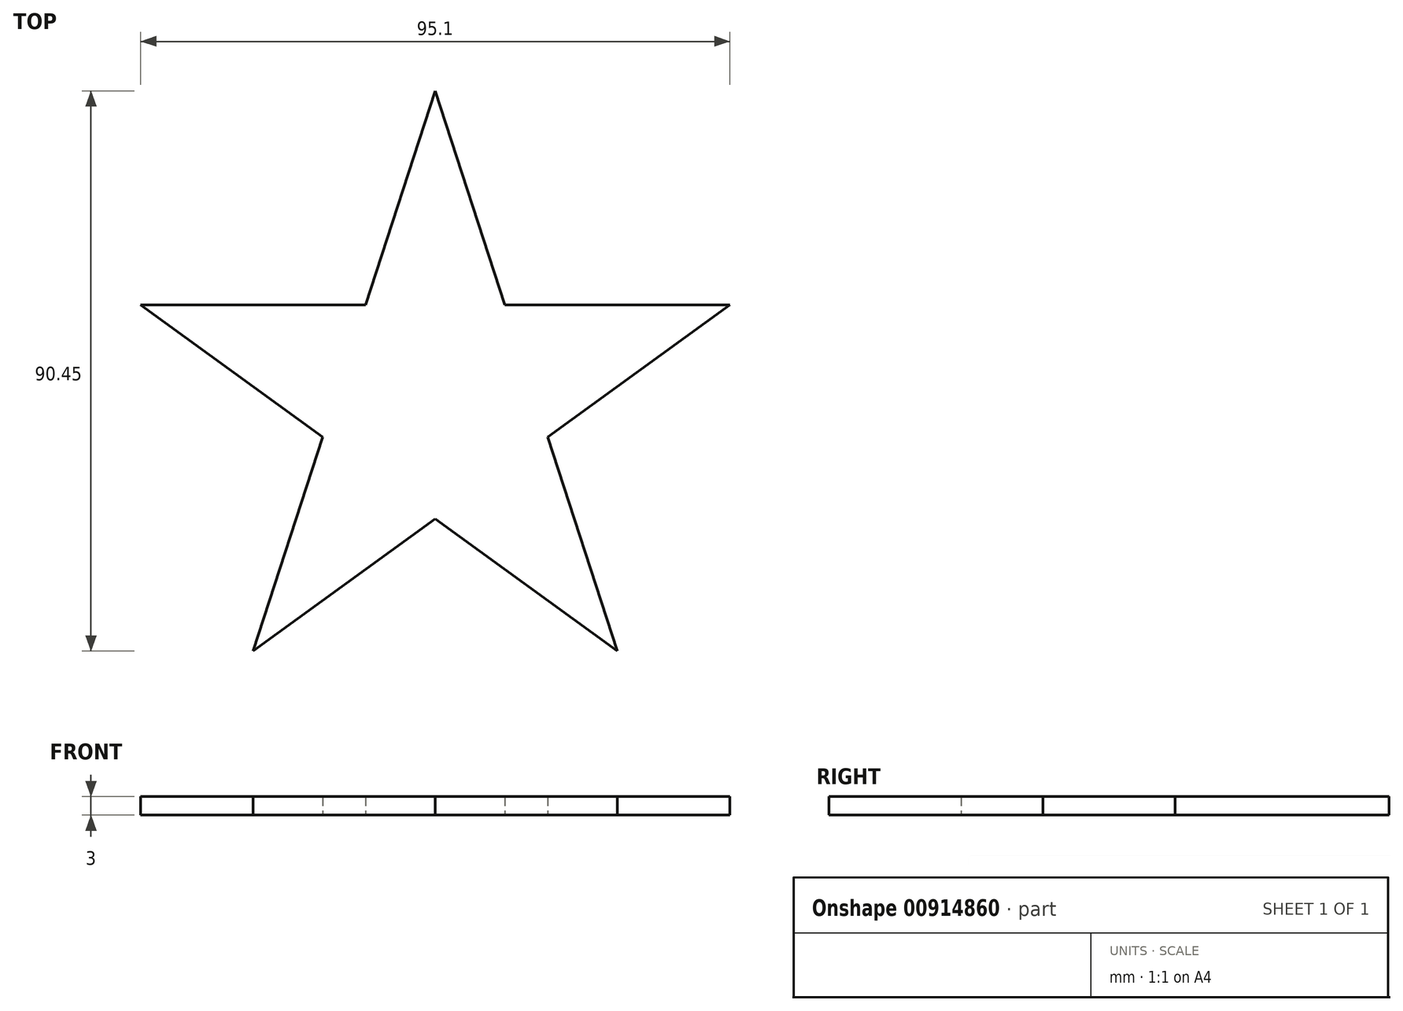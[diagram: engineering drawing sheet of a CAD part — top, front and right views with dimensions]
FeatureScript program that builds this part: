
annotation { "Feature Type Name" : "Feature", "Feature Type Description" : "" }
export const myFeature = defineFeature(function(context is Context, id is Id, definition is map)
    precondition{}
    {
        {
            var Q0;
            Q0=qCreatedBy(makeId("Top.planeOp"),FACE);
            var sketch = newSketch(context, id + "F0", { "sketchPlane" : qUnion([Q0])});
            skCircle(sketch, "E0", {"center": v(0, 0) * mm, "radius": 50 * mm});
            skPoint(sketch, "E1", {"position": v(0, 50) * mm});
            skPoint(sketch, "E2", {"position": v(47.55, 15.45) * mm});
            skPoint(sketch, "E3", {"position": v(29.39, -40.45) * mm});
            skPoint(sketch, "E4", {"position": v(-29.39, -40.45) * mm});
            skPoint(sketch, "E5", {"position": v(-47.55, 15.45) * mm});
            skLineSegment(sketch, "E6", {"start": v(0, 50) * mm, "end": v(0, 0) * mm});
            skLineSegment(sketch, "E7", {"start": v(47.55, 15.45) * mm, "end": v(0, 0) * mm});
            skLineSegment(sketch, "E8", {"start": v(29.39, -40.45) * mm, "end": v(0, 0) * mm});
            skLineSegment(sketch, "E9", {"start": v(-29.39, -40.45) * mm, "end": v(0, 0) * mm});
            skLineSegment(sketch, "E10", {"start": v(-47.55, 15.45) * mm, "end": v(0, 0) * mm});
            skLineSegment(sketch, "E11", {"start": v(-29.39, -40.45) * mm, "end": v(0, 50) * mm});
            skLineSegment(sketch, "E12", {"start": v(0, 50) * mm, "end": v(29.39, -40.45) * mm});
            skLineSegment(sketch, "E13", {"start": v(29.39, -40.45) * mm, "end": v(-47.55, 15.45) * mm});
            skLineSegment(sketch, "E14", {"start": v(-47.55, 15.45) * mm, "end": v(47.55, 15.45) * mm});
            skLineSegment(sketch, "E15", {"start": v(47.55, 15.45) * mm, "end": v(-29.39, -40.45) * mm});
            skSolve(sketch);
        }
        {
            var Q0;
            {var subQ1=sQuery(id+"F0.wireOp",EDGE,"E6");var subQ3=sQuery(id+"F0.wireOp",EDGE,"E14");var subQ4=makeQuery(id+"F0.imprint","INTERSECT",VERTEX,{"derivedFrom":[subQ1,subQ3]});Q0=makeQuery(id+"F0.imprint","IMPRINT",FACE,{"disambiguationData":[TD([[makeQuery(id+"F0.imprint","IMPRINT",EDGE,{"disambiguationData":[TD([[subQ4,1.0]])],"derivedFrom":subQ3}),1.0]])]});}
            var Q1;
            {var subQ1=sQuery(id+"F0.wireOp",EDGE,"E6");var subQ3=sQuery(id+"F0.wireOp",EDGE,"E14");var subQ4=makeQuery(id+"F0.imprint","INTERSECT",VERTEX,{"derivedFrom":[subQ1,subQ3]});Q1=makeQuery(id+"F0.imprint","IMPRINT",FACE,{"disambiguationData":[TD([[makeQuery(id+"F0.imprint","IMPRINT",EDGE,{"disambiguationData":[TD([[subQ4,-1.0]])],"derivedFrom":subQ3}),1.0]])]});}
            var Q2;
            {var subQ1=sQuery(id+"F0.wireOp",EDGE,"E7");var subQ3=sQuery(id+"F0.wireOp",EDGE,"E12");var subQ4=makeQuery(id+"F0.imprint","INTERSECT",VERTEX,{"derivedFrom":[subQ1,subQ3]});Q2=makeQuery(id+"F0.imprint","IMPRINT",FACE,{"disambiguationData":[TD([[makeQuery(id+"F0.imprint","IMPRINT",EDGE,{"disambiguationData":[TD([[subQ4,1.0]])],"derivedFrom":subQ3}),1.0]])]});}
            var Q3;
            {var subQ1=sQuery(id+"F0.wireOp",EDGE,"E7");var subQ3=sQuery(id+"F0.wireOp",EDGE,"E12");var subQ4=makeQuery(id+"F0.imprint","INTERSECT",VERTEX,{"derivedFrom":[subQ1,subQ3]});Q3=makeQuery(id+"F0.imprint","IMPRINT",FACE,{"disambiguationData":[TD([[makeQuery(id+"F0.imprint","IMPRINT",EDGE,{"disambiguationData":[TD([[subQ4,-1.0]])],"derivedFrom":subQ3}),1.0]])]});}
            var Q4;
            {var subQ1=sQuery(id+"F0.wireOp",EDGE,"E8");var subQ3=sQuery(id+"F0.wireOp",EDGE,"E15");var subQ4=makeQuery(id+"F0.imprint","INTERSECT",VERTEX,{"derivedFrom":[subQ1,subQ3]});Q4=makeQuery(id+"F0.imprint","IMPRINT",FACE,{"disambiguationData":[TD([[makeQuery(id+"F0.imprint","IMPRINT",EDGE,{"disambiguationData":[TD([[subQ4,1.0]])],"derivedFrom":subQ3}),1.0]])]});}
            var Q5;
            {var subQ1=sQuery(id+"F0.wireOp",EDGE,"E8");var subQ3=sQuery(id+"F0.wireOp",EDGE,"E15");var subQ4=makeQuery(id+"F0.imprint","INTERSECT",VERTEX,{"derivedFrom":[subQ1,subQ3]});Q5=makeQuery(id+"F0.imprint","IMPRINT",FACE,{"disambiguationData":[TD([[makeQuery(id+"F0.imprint","IMPRINT",EDGE,{"disambiguationData":[TD([[subQ4,-1.0]])],"derivedFrom":subQ3}),1.0]])]});}
            var Q6;
            {var subQ1=sQuery(id+"F0.wireOp",EDGE,"E9");var subQ3=sQuery(id+"F0.wireOp",EDGE,"E13");var subQ4=makeQuery(id+"F0.imprint","INTERSECT",VERTEX,{"derivedFrom":[subQ1,subQ3]});Q6=makeQuery(id+"F0.imprint","IMPRINT",FACE,{"disambiguationData":[TD([[makeQuery(id+"F0.imprint","IMPRINT",EDGE,{"disambiguationData":[TD([[subQ4,-1.0]])],"derivedFrom":subQ3}),1.0]])]});}
            var Q7;
            {var subQ1=sQuery(id+"F0.wireOp",EDGE,"E9");var subQ3=sQuery(id+"F0.wireOp",EDGE,"E13");var subQ4=makeQuery(id+"F0.imprint","INTERSECT",VERTEX,{"derivedFrom":[subQ1,subQ3]});Q7=makeQuery(id+"F0.imprint","IMPRINT",FACE,{"disambiguationData":[TD([[makeQuery(id+"F0.imprint","IMPRINT",EDGE,{"disambiguationData":[TD([[subQ4,1.0]])],"derivedFrom":subQ3}),1.0]])]});}
            var Q8;
            {var subQ1=sQuery(id+"F0.wireOp",EDGE,"E10");var subQ3=sQuery(id+"F0.wireOp",EDGE,"E11");var subQ4=makeQuery(id+"F0.imprint","INTERSECT",VERTEX,{"derivedFrom":[subQ1,subQ3]});Q8=makeQuery(id+"F0.imprint","IMPRINT",FACE,{"disambiguationData":[TD([[makeQuery(id+"F0.imprint","IMPRINT",EDGE,{"disambiguationData":[TD([[subQ4,1.0]])],"derivedFrom":subQ3}),1.0]])]});}
            var Q9;
            {var subQ1=sQuery(id+"F0.wireOp",EDGE,"E10");var subQ3=sQuery(id+"F0.wireOp",EDGE,"E11");var subQ4=makeQuery(id+"F0.imprint","INTERSECT",VERTEX,{"derivedFrom":[subQ1,subQ3]});Q9=makeQuery(id+"F0.imprint","IMPRINT",FACE,{"disambiguationData":[TD([[makeQuery(id+"F0.imprint","IMPRINT",EDGE,{"disambiguationData":[TD([[subQ4,-1.0]])],"derivedFrom":subQ3}),1.0]])]});}
            var Q10;
            {var subQ0=sQuery(id+"F0.wireOp",EDGE,"E7");var subQ5=sQuery(id+"F0.wireOp",EDGE,"E12");var subQ6=makeQuery(id+"F0.imprint","INTERSECT",VERTEX,{"derivedFrom":[subQ0,subQ5]});Q10=makeQuery(id+"F0.imprint","IMPRINT",FACE,{"disambiguationData":[TD([[makeQuery(id+"F0.imprint","IMPRINT",EDGE,{"disambiguationData":[TD([[subQ6,1.0]])],"derivedFrom":subQ5}),-1.0]])]});}
            var Q11;
            {var subQ0=sQuery(id+"F0.wireOp",EDGE,"E10");var subQ5=sQuery(id+"F0.wireOp",EDGE,"E11");var subQ6=makeQuery(id+"F0.imprint","INTERSECT",VERTEX,{"derivedFrom":[subQ0,subQ5]});Q11=makeQuery(id+"F0.imprint","IMPRINT",FACE,{"disambiguationData":[TD([[makeQuery(id+"F0.imprint","IMPRINT",EDGE,{"disambiguationData":[TD([[subQ6,-1.0]])],"derivedFrom":subQ5}),-1.0]])]});}
            var Q12;
            {var subQ0=sQuery(id+"F0.wireOp",EDGE,"E10");var subQ5=sQuery(id+"F0.wireOp",EDGE,"E11");var subQ6=makeQuery(id+"F0.imprint","INTERSECT",VERTEX,{"derivedFrom":[subQ0,subQ5]});Q12=makeQuery(id+"F0.imprint","IMPRINT",FACE,{"disambiguationData":[TD([[makeQuery(id+"F0.imprint","IMPRINT",EDGE,{"disambiguationData":[TD([[subQ6,1.0]])],"derivedFrom":subQ5}),-1.0]])]});}
            var Q13;
            {var subQ0=sQuery(id+"F0.wireOp",EDGE,"E9");var subQ5=sQuery(id+"F0.wireOp",EDGE,"E13");var subQ6=makeQuery(id+"F0.imprint","INTERSECT",VERTEX,{"derivedFrom":[subQ0,subQ5]});Q13=makeQuery(id+"F0.imprint","IMPRINT",FACE,{"disambiguationData":[TD([[makeQuery(id+"F0.imprint","IMPRINT",EDGE,{"disambiguationData":[TD([[subQ6,1.0]])],"derivedFrom":subQ5}),-1.0]])]});}
            var Q14;
            {var subQ1=sQuery(id+"F0.wireOp",EDGE,"E7");var subQ3=sQuery(id+"F0.wireOp",EDGE,"E12");var subQ4=makeQuery(id+"F0.imprint","INTERSECT",VERTEX,{"derivedFrom":[subQ1,subQ3]});Q14=makeQuery(id+"F0.imprint","IMPRINT",FACE,{"disambiguationData":[TD([[makeQuery(id+"F0.imprint","IMPRINT",EDGE,{"disambiguationData":[TD([[subQ4,-1.0]])],"derivedFrom":subQ3}),-1.0]])]});}
            extrude(context, id + "F1", {"entities" : qUnion([Q0, Q1, Q2, Q3, Q4, Q5, Q6, Q7, Q8, Q9, Q10, Q11, Q12, Q13, Q14]), "depth" : 3 * mm, "offsetDistance" : 25 * mm});
        }
    });
